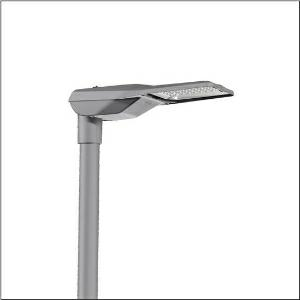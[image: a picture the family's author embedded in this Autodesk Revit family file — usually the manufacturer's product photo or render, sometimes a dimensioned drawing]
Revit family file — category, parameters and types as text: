
# Revit family: streetlight_sl_21_iq_mini___p0_8ab_5xe2r31v08gb_1261
name_source: partatom
category: Lighting Fixtures
units: mm (PartAtom-declared; Revit-internal decimal feet)

## family parameters
Cut with Voids When Loaded = No
Host = Face
Light Source = No
Part Type = Normal
Room Calculation Point = No
Round Connector Dimension = Use Diameter
Shared = No

## types (1)
- --- (1 x LED, 5200 lm, 39.8 W, 3000K)
    Apparent Load = 40 VA
    CIE Flux Codes = 36 71 98 100 100
    Color Rendering = 70
    Color Temperature = 3000K
    Default Elevation = 1800 mm
    Description = Streetlight SL 21 iQ mini, mast luminaire, primary light control with lens, of PMMA, primary optical cover: cover, of toughened safety glass, transparent, light distribution: P0.8aB, light emission: direct distribution, primary light characteristic: asymmetric, installation type: post-top, side-entry, LED, High Power LED, rated luminous flux: 5.200lm, luminous efficacy: 131lm/W, light colour: 730, colour temperature: 3000K, control gear: iQ-Street Remote, D4i with power reduction, control: pre-setting: logarithmic dimming characteristic, Street-Remote, Auto-Match, Temp-Guard, Lumen-Switch, Night-Set, Smart-Wire, Light-Fading, Desk-Remote (wireless, voltage-free reading and setting of iQ features in the workshop via application-optimized NFC function/RFID function), optimised constant luminous flux control (CLO 2.0), mains connection: 220..240V, AC, 50/60Hz, start of lifetime: 40W, end of service life: 41W, reduction: 18W, luminaire housing, of diecast aluminium, powder-coated, SITECO metallic grey (DB 702S), corrosivity category C5 high according to DIN EN ISO 12944, please order mast flange separately, inclination adjustable: 0°, 5°, 10°, 15°, sealing non-destructively replaceable, multi-level sealing system, length: 628mm, width: 235mm, height: 110mm, mast flange for spigot size: 42mm (side-entry): 5XC10008XM4, 60/48mm (side-entry/post-top): 5XC10108XM2, 76/60mm (side-entry/post-top): 5XC10108XM1, mounting height: 4..8m, Smart Interface above, protection rating (complete): IP66, insulation class (complete): insulation class II (safety insulation), certification: CE, ENEC, ENEC+, VDE, impact resistance: IK10, permissible operating ambient temperature for outdoor applications: -40..+50°C, standard-compliant lighting for roads and squares, packaging unit: 1 piece

Light Distribution: P0.8aB
    Height = 110 mm
    Lamp = 1 x LED
    Lamp Light Flux = 5200 lm
    Lamp Power = 39.8 W
    Lamp count = 1
    Length = 625 mm
    Luminous efficacy = 131 lm/W
    Manufacturer = Siteco
    ModVariant = No
    Model = 5XE2R31V08GB
    Number of Poles = 1
    OnlyDefault = Yes
    Power Factor = 1
    Product Name = Streetlight SL 21 iQ mini | P0.8aB
    Product group = mast luminaire | pylon top
    ProductGroupID = 6100
    Protection Class = Protection class II
    Protection Degree = IP 66
    RLX_Detail_Level = 1
    RLX_Emergency_Light_Flux = 0 lm
    RLX_Emergency_Type = 0
    RLX_Emergency_Type_DB = No
    RlxData = <blob elided: 92205 chars, md5=ab0f8ec6>
    Socket = socket
    Standby Power = 0 W
    System Light Flux = 5200 lm
    System Power = 40 W
    Type Comments = factory setting: luminous flux: 100 % | dim-lin: 254 | 800 mA
    Type Image = l_1003515.jpg
    URL = http://relux.com
    VarID = @adj_083167
    Voltage = 0 V
    Weight = 0.00 kg
    Width = 234 mm

## geometry (parser evidence)
native form markers: Blend x4, Sweep x11
no freeform markers — native parametric forms only
